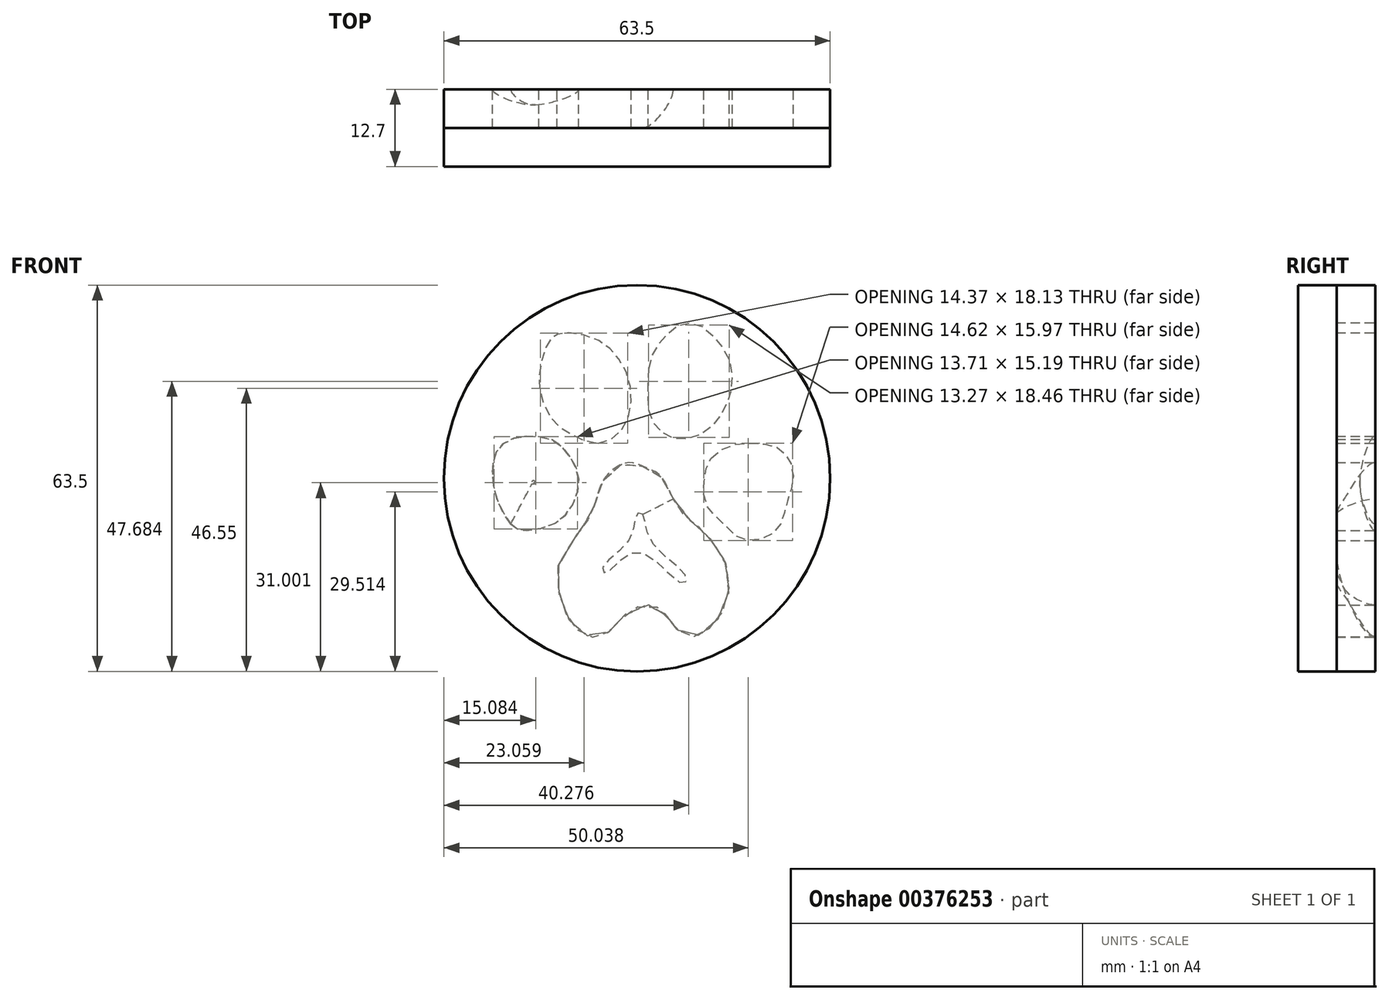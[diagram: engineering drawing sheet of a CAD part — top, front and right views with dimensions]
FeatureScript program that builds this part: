
annotation { "Feature Type Name" : "Feature", "Feature Type Description" : "" }
export const myFeature = defineFeature(function(context is Context, id is Id, definition is map)
    precondition{}
    {
        {
            var Q0;
            Q0=qCreatedBy(makeId("Front.planeOp"),FACE);
            var sketch = newSketch(context, id + "F0", { "sketchPlane" : qUnion([Q0])});
            skCircle(sketch, "E0", {"center": v(0, 0) * mm, "radius": 27.43 * mm});
            skSolve(sketch);
        }
        {
            var Q0;
            Q0=qCreatedBy(makeId("Front.planeOp"),FACE);
            var sketch = newSketch(context, id + "F1", { "sketchPlane" : qUnion([Q0])});
            skFitSpline(sketch, "E1", {"points": [v(-6.36, 5.73) * mm, v(-2.73, 7.69) * mm, v(-1.05, 11.74) * mm, v(-1.54, 16.83) * mm, v(-3.85, 20.67) * mm, v(-7.2, 23.05) * mm, v(-12.09, 23.89) * mm, v(-13.7, 23.33) * mm, v(-14.74, 22) * mm, v(-16, 17.67) * mm, v(-15.79, 13.62) * mm, v(-13.76, 9.43) * mm, v(-10.61, 7.13) * mm, v(-6.36, 5.73) * mm]});
            skSolve(sketch);
        }
        {
            var Q0;
            Q0=qCreatedBy(makeId("Front.planeOp"),FACE);
            var sketch = newSketch(context, id + "F2", { "sketchPlane" : qUnion([Q0])});
            skFitSpline(sketch, "E2", {"points": [v(1.95, 18) * mm, v(2.95, 21.12) * mm, v(5.3, 24) * mm, v(7.55, 25.44) * mm, v(10.52, 25.05) * mm, v(13.17, 22.64) * mm, v(15.27, 19.22) * mm, v(15.51, 14.79) * mm, v(14.44, 11.57) * mm, v(12.28, 8.54) * mm, v(9.34, 6.71) * mm, v(6.23, 6.52) * mm, v(3.51, 8.05) * mm, v(1.98, 10.91) * mm, v(1.84, 14.86) * mm, v(1.95, 18) * mm]});
            skSolve(sketch);
        }
        {
            var Q0;
            Q0=qCreatedBy(makeId("Front.planeOp"),FACE);
            var sketch = newSketch(context, id + "F3", { "sketchPlane" : qUnion([Q0])});
            skFitSpline(sketch, "E3", {"points": [v(-20.76, -7.52) * mm, v(-22.43, -4.82) * mm, v(-23.66, -0.88) * mm, v(-23.63, 2.35) * mm, v(-23.18, 4.27) * mm, v(-21.66, 5.9) * mm, v(-19.07, 6.84) * mm, v(-15.5, 6.73) * mm, v(-12.97, 5.73) * mm, v(-10.91, 3.32) * mm, v(-9.74, 0.8) * mm, v(-9.8, -2.26) * mm, v(-11.27, -5.43) * mm, v(-13.73, -7.54) * mm, v(-17.84, -8.6) * mm, v(-19.66, -8.36) * mm, v(-20.76, -7.52) * mm]});
            skSolve(sketch);
        }
        {
            var Q0;
            Q0=qCreatedBy(makeId("Front.planeOp"),FACE);
            var sketch = newSketch(context, id + "F4", { "sketchPlane" : qUnion([Q0])});
            skFitSpline(sketch, "E4", {"points": [v(12.17, 3.3) * mm, v(15.24, 5.3) * mm, v(18.85, 5.75) * mm, v(22.63, 5.25) * mm, v(24.33, 4) * mm, v(25.46, 1.89) * mm, v(25.58, -1.06) * mm, v(24.67, -3.93) * mm, v(23.96, -6.62) * mm, v(22.67, -8.78) * mm, v(19.69, -10.2) * mm, v(16.65, -9.74) * mm, v(14.12, -7.37) * mm, v(11.8, -5.05) * mm, v(10.97, -2.3) * mm, v(11.22, 0.93) * mm, v(12.17, 3.3) * mm]});
            skSolve(sketch);
        }
        {
            var Q0;
            Q0=qCreatedBy(makeId("Front.planeOp"),FACE);
            var sketch = newSketch(context, id + "F5", { "sketchPlane" : qUnion([Q0])});
            skFitSpline(sketch, "E5", {"points": [v(-6.97, -4.43) * mm, v(-5.72, -0.6) * mm, v(-3.15, 1.97) * mm, v(-0.99, 2.55) * mm, v(1.75, 1.63) * mm, v(3.84, 0.4) * mm, v(5.76, -2.92) * mm, v(7.68, -5.93) * mm, v(10.47, -8.33) * mm, v(13.47, -11.9) * mm, v(15.13, -16.09) * mm, v(14.22, -21.67) * mm, v(11.78, -24.75) * mm, v(9.4, -26.02) * mm, v(6.67, -24.91) * mm, v(5.11, -23.18) * mm, v(4.18, -21.78) * mm, v(1.56, -20.84) * mm, v(-1.77, -22.24) * mm, v(-3.75, -24.52) * mm, v(-6.43, -26.07) * mm, v(-8.94, -25.53) * mm, v(-11, -23.57) * mm, v(-12.78, -19.02) * mm, v(-12.98, -14.5) * mm, v(-11.48, -11.85) * mm, v(-9.96, -9.35) * mm, v(-7.96, -6.65) * mm, v(-6.97, -4.43) * mm]});
            skSolve(sketch);
        }
        {
            var Q0;
            Q0=qCreatedBy(makeId("Front.planeOp"),FACE);
            cPlane(context, id + "F6", {"entities" : qUnion([Q0]), "cplaneType" : CPlaneType.OFFSET, "offset" : 6.35 * mm, "width" : 152.4 * mm, "height" : 152.4 * mm});
        }
        {
            var Q0;
            Q0=qCreatedBy(id+"F6.planeOp",FACE);
            cPlane(context, id + "F7", {"entities" : qUnion([Q0]), "cplaneType" : CPlaneType.OFFSET, "offset" : 3.8 * mm, "oppositeDirection" : true, "width" : 152.4 * mm, "height" : 152.4 * mm});
        }
        {
            var Q0;
            Q0=qCreatedBy(id+"F6.planeOp",FACE);
            var sketch = newSketch(context, id + "F8", { "sketchPlane" : qUnion([Q0])});
            skFitSpline(sketch, "E6", {"points": [v(0.95, -5.94) * mm, v(0, -5.81) * mm, v(-1.17, -9.9) * mm, v(-5.7, -14.8) * mm, v(-5.13, -15.54) * mm, v(0, -12.07) * mm, v(7.35, -17.22) * mm, v(8.13, -16.35) * mm, v(2.27, -10.27) * mm, v(0.95, -5.94) * mm]});
            skSolve(sketch);
        }
        {
            var Q0;
            Q0=qCreatedBy(makeId("Front.planeOp"),FACE);
            var sketch = newSketch(context, id + "F9", { "sketchPlane" : qUnion([Q0])});
            skCircle(sketch, "E7", {"center": v(0, 0) * mm, "radius": 31.75 * mm});
            skSolve(sketch);
        }
        {
            var Q0;
            Q0=qCreatedBy(id+"F7.planeOp",FACE);
            var sketch = newSketch(context, id + "F10", { "sketchPlane" : qUnion([Q0])});
            skFitSpline(sketch, "E8", {"points": [v(-16.78, -0.54) * mm, v(-16.82, -0.46) * mm, v(-16.93, -0.41) * mm, v(-17.08, -0.4) * mm, v(-17.23, -0.46) * mm, v(-17.3, -0.55) * mm, v(-17.32, -0.67) * mm, v(-17.28, -0.85) * mm, v(-17.17, -0.9) * mm, v(-16.98, -0.94) * mm, v(-16.83, -0.86) * mm, v(-16.74, -0.71) * mm, v(-16.78, -0.54) * mm]});
            skSolve(sketch);
        }
        {
            var Q0;
            Q0=makeQuery(id+"F9.imprint","IMPRINT",FACE,{"disambiguationData":[TD([[makeQuery(id+"F9.imprint","IMPRINT",EDGE,{"derivedFrom":sQuery(id+"F9.wireOp",EDGE,"E7")}),1.0]])]});
            var Q1;
            Q1=sQuery(id+"F9.wireOp",EDGE,"E7");
            extrude(context, id + "F11", {"entities" : qUnion([Q0]), "surfaceEntities" : qUnion([Q1]), "depth" : 6.35 * mm});
        }
        {
            var Q0;
            Q0 = qSketchRegion(id + "F1", true);
            var Q1;
            Q1 = qSketchRegion(id + "F2", true);
            var Q2;
            Q2 = qSketchRegion(id + "F3", true);
            var Q3;
            Q3 = qSketchRegion(id + "F4", true);
            var Q4;
            Q4 = qSketchRegion(id + "F5", true);
            var Q5;
            Q5=sQuery(id+"F2.wireOp",EDGE,"E2");
            extrude(context, id + "F12", {"entities" : qUnion([Q0, Q1, Q2, Q3, Q4]), "operationType" : NewBodyOperationType.REMOVE, "surfaceEntities" : qUnion([Q5]), "depth" : 25.4 * mm});
        }
        {
            var Q0;
            Q0 = qSketchRegion(id + "F9", true);
            extrude(context, id + "F13", {"entities" : qUnion([Q0]), "depth" : 12.7 * mm});
        }
        {
            var Q1;
            Q1 = qSketchRegion(id + "F8", true);
            var Q2;
            Q2 = qSketchRegion(id + "F5", true);
            loft(context, id + "F14", {"operationType" : NewBodyOperationType.REMOVE, "startCondition" : LoftEndDerivativeType.TANGENT_TO_PROFILE, "startMagnitude" : 1, "endCondition" : LoftEndDerivativeType.NORMAL_TO_PROFILE, "endMagnitude" : 1, "sheetProfilesArray" : [{ "sheetProfileEntities" : qUnion([Q1]) }, { "sheetProfileEntities" : qUnion([Q2]) }]});
        }
        {
            var Q1;
            Q1 = qSketchRegion(id + "F3", true);
            var Q2;
            Q2 = qSketchRegion(id + "F10", true);
            loft(context, id + "F15", {"operationType" : NewBodyOperationType.REMOVE, "startCondition" : LoftEndDerivativeType.NORMAL_TO_PROFILE, "startMagnitude" : 1, "endCondition" : LoftEndDerivativeType.TANGENT_TO_PROFILE, "endMagnitude" : 1, "sheetProfilesArray" : [{ "sheetProfileEntities" : qUnion([Q1]) }, { "sheetProfileEntities" : qUnion([Q2]) }]});
        }
    });
